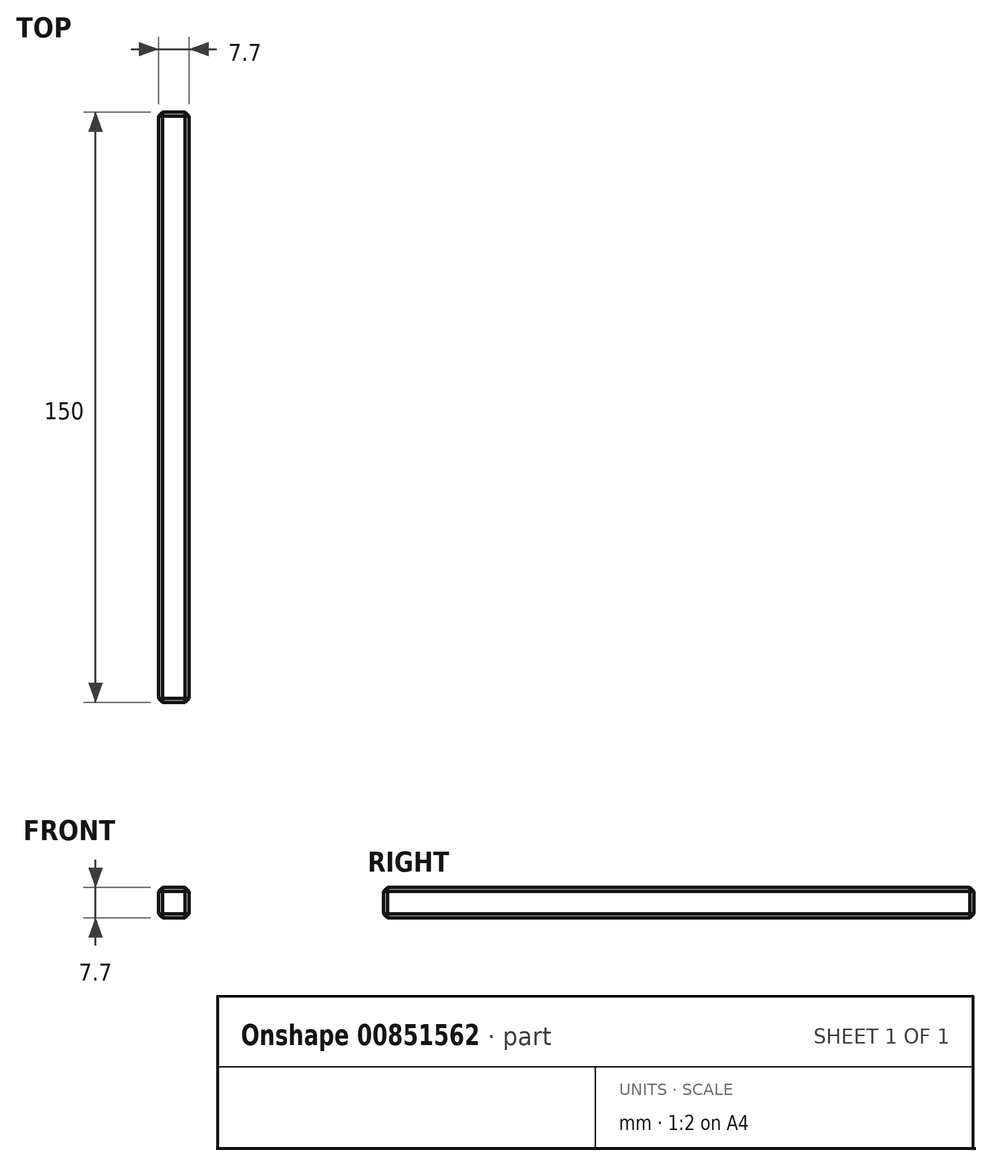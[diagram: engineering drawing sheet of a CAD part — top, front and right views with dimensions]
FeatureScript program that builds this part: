
annotation { "Feature Type Name" : "Feature", "Feature Type Description" : "" }
export const myFeature = defineFeature(function(context is Context, id is Id, definition is map)
    precondition{}
    {
        {
            var Q0;
            Q0=qCreatedBy(makeId("Top.planeOp"),FACE);
            var sketch = newSketch(context, id + "F0", { "sketchPlane" : qUnion([Q0])});
            skLineSegment(sketch, "E0.bottom", {"start": v(11, -75) * mm, "end": v(18.7, -75) * mm});
            skLineSegment(sketch, "E0.top", {"start": v(11, 75) * mm, "end": v(18.7, 75) * mm});
            skLineSegment(sketch, "E0.left", {"start": v(11, -75) * mm, "end": v(11, 75) * mm});
            skLineSegment(sketch, "E0.right", {"start": v(18.7, -75) * mm, "end": v(18.7, 75) * mm});
            skSolve(sketch);
        }
        {
            var Q0;
            Q0=makeQuery(id+"F0.imprint","IMPRINT",FACE,{"disambiguationData":[TD([[makeQuery(id+"F0.imprint","IMPRINT",EDGE,{"derivedFrom":sQuery(id+"F0.wireOp",EDGE,"E0.bottom")}),1.0]])]});
            extrude(context, id + "F1", {"entities" : qUnion([Q0]), "depth" : 7.7 * mm, "offsetDistance" : 25 * mm});
        }
        {
            var Q0;
            Q0=makeQuery(id+"F1.opExtrude","SWEPT_FACE",FACE,{"disambiguationData":[OSD([sQuery(id+"F0.wireOp",EDGE,"E0.bottom")])]});
            var Q1;
            Q1=makeQuery(id+"F1.opExtrude","SWEPT_FACE",FACE,{"disambiguationData":[OSD([sQuery(id+"F0.wireOp",EDGE,"E0.right")])]});
            var Q2;
            Q2=makeQuery(id+"F1.opExtrude","CAP_FACE",FACE,{"disambiguationData":[OSD([sQuery(id+"F0.wireOp",EDGE,"E0.bottom"),sQuery(id+"F0.wireOp",EDGE,"E0.top"),sQuery(id+"F0.wireOp",EDGE,"E0.left"),sQuery(id+"F0.wireOp",EDGE,"E0.right")])],"isStart":true});
            var Q3;
            Q3=makeQuery(id+"F1.opExtrude","SWEPT_FACE",FACE,{"disambiguationData":[OSD([sQuery(id+"F0.wireOp",EDGE,"E0.left")])]});
            var Q4;
            Q4=makeQuery(id+"F1.opExtrude","CAP_FACE",FACE,{"disambiguationData":[OSD([sQuery(id+"F0.wireOp",EDGE,"E0.bottom"),sQuery(id+"F0.wireOp",EDGE,"E0.top"),sQuery(id+"F0.wireOp",EDGE,"E0.left"),sQuery(id+"F0.wireOp",EDGE,"E0.right")])],"isStart":false});
            chamfer(context, id + "F2", {"entities" : qUnion([Q0, Q1, Q2, Q3, Q4]), "width" : 1 * mm, "tangentPropagation" : true});
        }
    });
